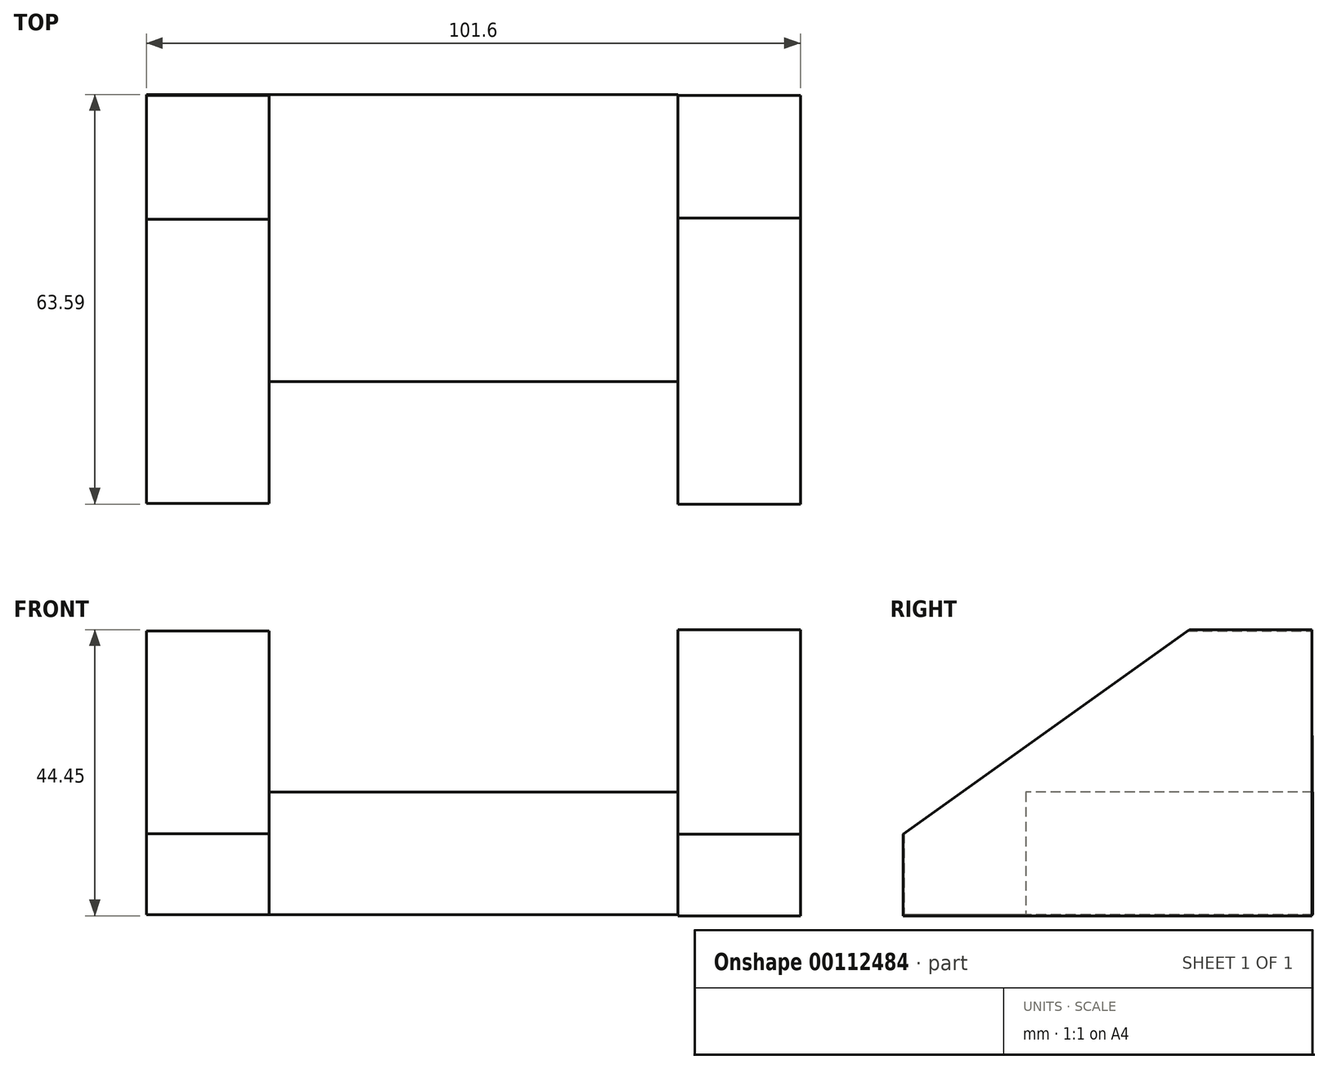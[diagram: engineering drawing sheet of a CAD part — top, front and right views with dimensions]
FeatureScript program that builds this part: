
annotation { "Feature Type Name" : "Feature", "Feature Type Description" : "" }
export const myFeature = defineFeature(function(context is Context, id is Id, definition is map)
    precondition{}
    {
        {
            var Q0;
            Q0=qCreatedBy(makeId("Right.planeOp"),FACE);
            var sketch = newSketch(context, id + "F0", { "sketchPlane" : qUnion([Q0])});
            skLineSegment(sketch, "E0", {"start": v(-3.74, 20.6) * mm, "end": v(15.31, 20.6) * mm});
            skLineSegment(sketch, "E1", {"start": v(15.31, 20.6) * mm, "end": v(15.31, -23.85) * mm});
            skLineSegment(sketch, "E2", {"start": v(15.31, -23.85) * mm, "end": v(-48.19, -23.85) * mm});
            skLineSegment(sketch, "E3", {"start": v(-48.19, -23.85) * mm, "end": v(-48.19, -11.15) * mm});
            skLineSegment(sketch, "E4", {"start": v(-48.19, -11.15) * mm, "end": v(-3.74, 20.6) * mm});
            skSolve(sketch);
        }
        {
            var Q0;
            Q0=makeQuery(id+"F0.imprint","IMPRINT",FACE,{"disambiguationData":[TD([[makeQuery(id+"F0.imprint","IMPRINT",EDGE,{"derivedFrom":sQuery(id+"F0.wireOp",EDGE,"E0")}),-1.0]])]});
            extrude(context, id + "F1", {"entities" : qUnion([Q0]), "depth" : 19.05 * mm});
        }
        {
            var Q0;
            Q0=qCreatedBy(makeId("Right.planeOp"),FACE);
            var sketch = newSketch(context, id + "F2", { "sketchPlane" : qUnion([Q0])});
            skLineSegment(sketch, "E5", {"start": v(15.4, -23.71) * mm, "end": v(-29.14, -23.71) * mm});
            skLineSegment(sketch, "E6", {"start": v(15.4, -23.71) * mm, "end": v(15.4, -4.65) * mm});
            skLineSegment(sketch, "E7", {"start": v(15.4, -4.65) * mm, "end": v(-29.14, -4.65) * mm});
            skLineSegment(sketch, "E8", {"start": v(-29.14, -4.65) * mm, "end": v(-29.14, -23.71) * mm});
            skSolve(sketch);
        }
        {
            var Q0;
            Q0 = qSketchRegion(id + "F2", true);
            extrude(context, id + "F3", {"entities" : qUnion([Q0]), "oppositeDirection" : true, "depth" : 63.5 * mm});
        }
        {
            var Q0;
            Q0=makeQuery(id+"F3.opExtrude","CAP_FACE",FACE,{"disambiguationData":[OSD([sQuery(id+"F2.wireOp",EDGE,"E5"),sQuery(id+"F2.wireOp",EDGE,"E6"),sQuery(id+"F2.wireOp",EDGE,"E7"),sQuery(id+"F2.wireOp",EDGE,"E8")])],"isStart":false});
            var sketch = newSketch(context, id + "F4", { "sketchPlane" : qUnion([Q0])});
            skLineSegment(sketch, "E9", {"start": v(-15.4, -23.71) * mm, "end": v(48.1, -23.71) * mm});
            skLineSegment(sketch, "E10", {"start": v(48.1, -11.08) * mm, "end": v(48.1, -23.71) * mm});
            skLineSegment(sketch, "E11", {"start": v(48.1, -11.08) * mm, "end": v(3.99, 20.4) * mm});
            skLineSegment(sketch, "E12", {"start": v(3.99, 20.4) * mm, "end": v(-15.3, 20.4) * mm});
            skLineSegment(sketch, "E13", {"start": v(-15.3, 20.4) * mm, "end": v(-15.4, -23.71) * mm});
            skSolve(sketch);
        }
        {
            var Q0;
            {var subQ1=sQuery(id+"F4.wireOp",EDGE,"E10");Q0=makeQuery(id+"F4.imprint","IMPRINT",FACE,{"disambiguationData":[TD([[makeQuery(id+"F4.imprint","IMPRINT",EDGE,{"derivedFrom":subQ1}),-1.0]])]});}
            var Q1;
            {var subQ3=makeQuery(id+"F3.opExtrude","CAP_EDGE",EDGE,{"disambiguationData":[OSD([sQuery(id+"F2.wireOp",EDGE,"E8")])],"isStart":false});Q1=makeQuery(id+"F4.imprint","IMPRINT",FACE,{"disambiguationData":[TD([[makeQuery(id+"F4.imprint","IMPRINT",EDGE,{"derivedFrom":subQ3}),-1.0]])]});}
            extrude(context, id + "F5", {"entities" : qUnion([Q0, Q1]), "operationType" : NewBodyOperationType.ADD, "depth" : 19.05 * mm});
        }
    });
